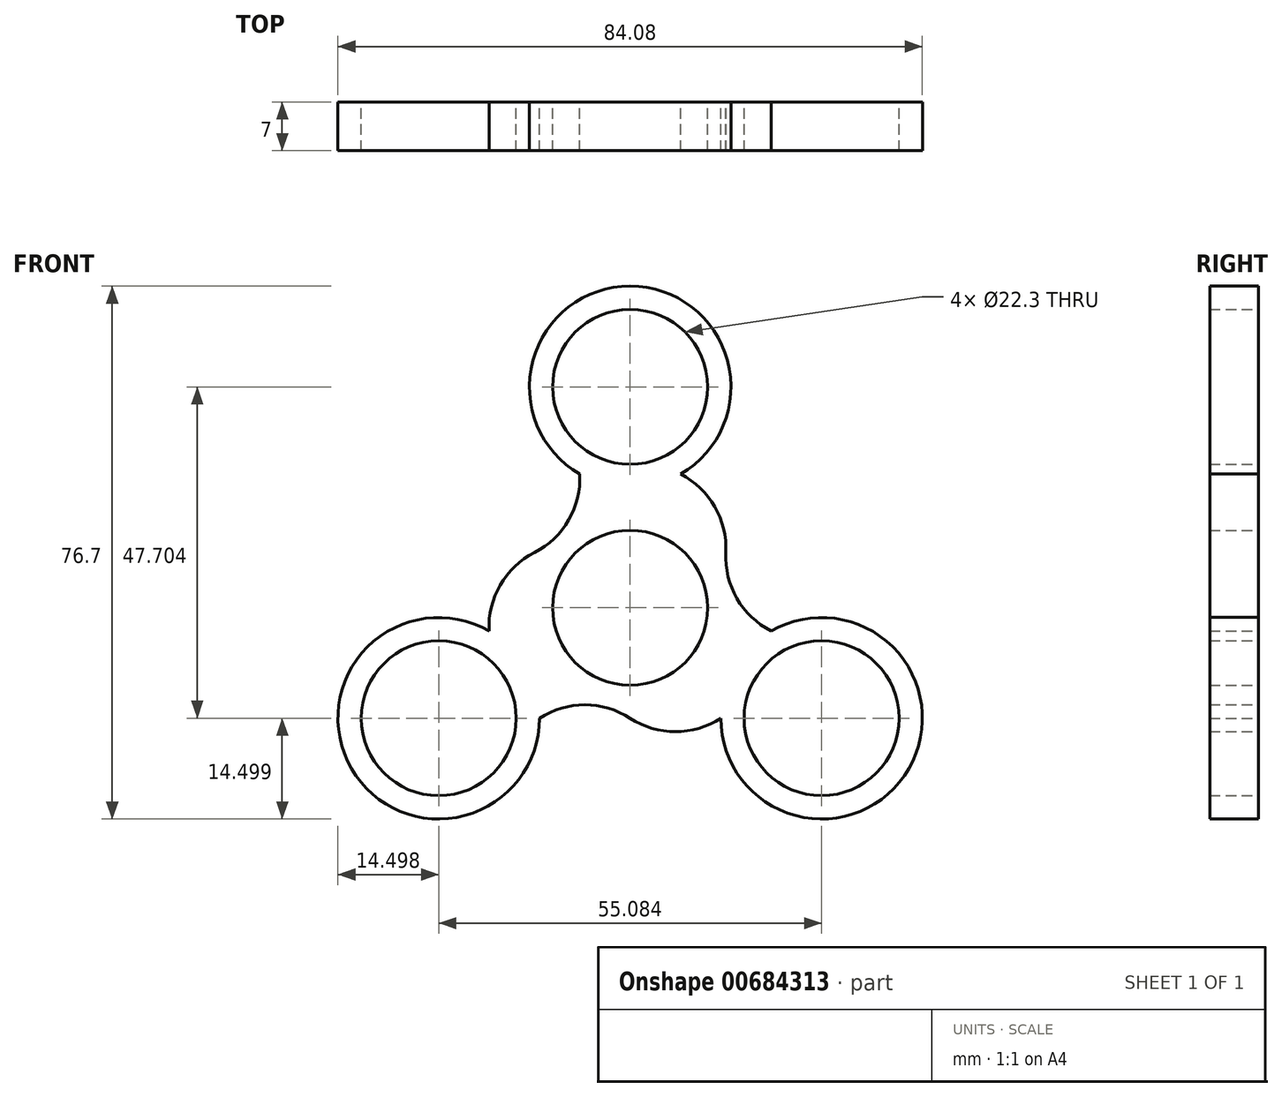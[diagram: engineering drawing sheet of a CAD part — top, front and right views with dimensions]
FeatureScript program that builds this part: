
annotation { "Feature Type Name" : "Feature", "Feature Type Description" : "" }
export const myFeature = defineFeature(function(context is Context, id is Id, definition is map)
    precondition{}
    {
        {
            var Q0;
            Q0=qCreatedBy(makeId("Front.planeOp"),FACE);
            var sketch = newSketch(context, id + "F0", { "sketchPlane" : qUnion([Q0])});
            skCircle(sketch, "E0", {"center": v(0, 0) * mm, "radius": 11.15 * mm});
            skCircle(sketch, "E1", {"center": v(0, 31.8) * mm, "radius": 11.15 * mm});
            skCircle(sketch, "E2", {"center": v(0, 31.8) * mm, "radius": 14.5 * mm});
            skCircle(sketch, "E3.1.0", {"center": v(-27.54, -15.9) * mm, "radius": 11.15 * mm});
            skCircle(sketch, "E3.1.1", {"center": v(-27.54, -15.9) * mm, "radius": 14.5 * mm});
            skCircle(sketch, "E3.2.0", {"center": v(27.54, -15.9) * mm, "radius": 11.15 * mm});
            skCircle(sketch, "E3.2.1", {"center": v(27.54, -15.9) * mm, "radius": 14.5 * mm});
            skLineSegment(sketch, "E4", {"start": v(0, 31.8) * mm, "end": v(27.54, -15.9) * mm, "construction": true});
            skLineSegment(sketch, "E5", {"start": v(-27.54, -15.9) * mm, "end": v(0, 0) * mm, "construction": true});
            skLineSegment(sketch, "E6", {"start": v(0, 0) * mm, "end": v(27.54, 15.9) * mm, "construction": true});
            skArc(sketch, "E7", {"start": v(13.77, 7.95) * mm, "mid": v(15.36, 1.34) * mm, "end": v(20.3, -3.34) * mm});
            skArc(sketch, "E8", {"start": v(13.77, 7.95) * mm, "mid": v(12.18, 14.56) * mm, "end": v(7.25, 19.25) * mm});
            skArc(sketch, "E9.1.0", {"start": v(-13.77, 7.95) * mm, "mid": v(-18.7, 3.27) * mm, "end": v(-20.3, -3.34) * mm});
            skArc(sketch, "E9.2.0", {"start": v(0, -15.9) * mm, "mid": v(6.52, -17.83) * mm, "end": v(13.04, -15.9) * mm});
            skArc(sketch, "E10.1.0", {"start": v(-13.77, 7.95) * mm, "mid": v(-8.84, 12.63) * mm, "end": v(-7.25, 19.25) * mm});
            skArc(sketch, "E10.2.0", {"start": v(0, -15.9) * mm, "mid": v(-6.52, -13.97) * mm, "end": v(-13.04, -15.9) * mm});
            skSolve(sketch);
        }
        {
            var Q0;
            Q0 = qSketchRegion(id + "F0", true);
            extrude(context, id + "F1", {"entities" : qUnion([Q0]), "depth" : 7 * mm, "offsetDistance" : 25 * mm});
        }
    });
